FCSTD DOCUMENT  (FreeCAD 0.19R24276 (Git))
Label: base-20x20
License: All rights reserved
LicenseURL: http://en.wikipedia.org/wiki/All_rights_reserved
objects: Sketcher::SketchObject×1, PartDesign::Body×1
note: 2 computed .brp shape members not serialized (recipe doc carries the construction recipe); baked Part::Feature solids carry a one-line shape summary decoded from their .brp

FEATURE [Sketcher::SketchObject] Sketch  label="v2020"
  FullyConstrained = true
  MapMode = 5
  Support = -> [XY_Plane]
  sketch-geometry (45):
    g0: Circle CenterX=0 CenterY=0 CenterZ=0 NormalX=0 NormalY=0 NormalZ=1 AngleXU=0 Radius=2.5
    g1: LineSegment StartX=-3 StartY=4 StartZ=0 EndX=3 EndY=4 EndZ=0
    g2: LineSegment StartX=3 StartY=4 StartZ=0 EndX=5.1 EndY=6.1 EndZ=0
    g3: LineSegment StartX=5.1 StartY=6.1 StartZ=0 EndX=5.1 EndY=8.2 EndZ=0
    g4: LineSegment StartX=5.1 StartY=8.2 StartZ=0 EndX=3 EndY=8.2 EndZ=0
    g5: LineSegment StartX=3 StartY=8.2 StartZ=0 EndX=4.8 EndY=10 EndZ=0
    g6: LineSegment StartX=4.8 StartY=10 StartZ=0 EndX=10 EndY=10 EndZ=0
    g7: LineSegment StartX=10 StartY=10 StartZ=0 EndX=10 EndY=4.8 EndZ=0
    g8: LineSegment StartX=10 StartY=4.8 StartZ=0 EndX=8.2 EndY=3 EndZ=0
    g9: LineSegment StartX=8.2 StartY=3 StartZ=0 EndX=8.2 EndY=5.1 EndZ=0
    g10: LineSegment StartX=8.2 StartY=5.1 StartZ=0 EndX=6.1 EndY=5.1 EndZ=0
    g11: LineSegment StartX=6.1 StartY=5.1 StartZ=0 EndX=4 EndY=3 EndZ=0
    g12: LineSegment StartX=4 StartY=3 StartZ=0 EndX=4 EndY=-3 EndZ=0
    g13: LineSegment StartX=4 StartY=-3 StartZ=0 EndX=6.1 EndY=-5.1 EndZ=0
    g14: LineSegment StartX=6.1 StartY=-5.1 StartZ=0 EndX=8.2 EndY=-5.1 EndZ=0
    g15: LineSegment StartX=8.2 StartY=-5.1 StartZ=0 EndX=8.2 EndY=-3 EndZ=0
    g16: LineSegment StartX=8.2 StartY=-3 StartZ=0 EndX=10 EndY=-4.8 EndZ=0
    g17: LineSegment StartX=10 StartY=-4.8 StartZ=0 EndX=10 EndY=-10 EndZ=0
    g18: LineSegment StartX=10 StartY=-10 StartZ=0 EndX=4.8 EndY=-10 EndZ=0
    g19: LineSegment StartX=4.8 StartY=-10 StartZ=0 EndX=3 EndY=-8.2 EndZ=0
    g20: LineSegment StartX=3 StartY=-8.2 StartZ=0 EndX=5.1 EndY=-8.2 EndZ=0
    g21: LineSegment StartX=5.1 StartY=-8.2 StartZ=0 EndX=5.1 EndY=-6.1 EndZ=0
    g22: LineSegment StartX=5.1 StartY=-6.1 StartZ=0 EndX=3 EndY=-4 EndZ=0
    g23: LineSegment StartX=3 StartY=-4 StartZ=0 EndX=-3 EndY=-4 EndZ=0
    g24: LineSegment StartX=-3 StartY=-4 StartZ=0 EndX=-5.1 EndY=-6.1 EndZ=0
    g25: LineSegment StartX=-5.1 StartY=-6.1 StartZ=0 EndX=-5.1 EndY=-8.2 EndZ=0
    g26: LineSegment StartX=-5.1 StartY=-8.2 StartZ=0 EndX=-3 EndY=-8.2 EndZ=0
    g27: LineSegment StartX=-3 StartY=-8.2 StartZ=0 EndX=-4.8 EndY=-10 EndZ=0
    g28: LineSegment StartX=-4.8 StartY=-10 StartZ=0 EndX=-10 EndY=-10 EndZ=0
    g29: LineSegment StartX=-10 StartY=-10 StartZ=0 EndX=-10 EndY=-4.8 EndZ=0
    g30: LineSegment StartX=-10 StartY=-4.8 StartZ=0 EndX=-8.2 EndY=-3 EndZ=0
    g31: LineSegment StartX=-8.2 StartY=-3 StartZ=0 EndX=-8.2 EndY=-5.1 EndZ=0
    g32: LineSegment StartX=-8.2 StartY=-5.1 StartZ=0 EndX=-6.1 EndY=-5.1 EndZ=0
    g33: LineSegment StartX=-6.1 StartY=-5.1 StartZ=0 EndX=-4 EndY=-3 EndZ=0
    g34: LineSegment StartX=-4 StartY=-3 StartZ=0 EndX=-4 EndY=3 EndZ=0
    g35: LineSegment StartX=-4 StartY=3 StartZ=0 EndX=-6.1 EndY=5.1 EndZ=0
    g36: LineSegment StartX=-6.1 StartY=5.1 StartZ=0 EndX=-8.2 EndY=5.1 EndZ=0
    g37: LineSegment StartX=-8.2 StartY=5.1 StartZ=0 EndX=-8.2 EndY=3 EndZ=0
    g38: LineSegment StartX=-8.2 StartY=3 StartZ=0 EndX=-10 EndY=4.8 EndZ=0
    g39: LineSegment StartX=-10 StartY=4.8 StartZ=0 EndX=-10 EndY=10 EndZ=0
    g40: LineSegment StartX=-10 StartY=10 StartZ=0 EndX=-4.8 EndY=10 EndZ=0
    g41: LineSegment StartX=-4.8 StartY=10 StartZ=0 EndX=-3 EndY=8.2 EndZ=0
    g42: LineSegment StartX=-3 StartY=8.2 StartZ=0 EndX=-5.1 EndY=8.2 EndZ=0
    g43: LineSegment StartX=-5.1 StartY=8.2 StartZ=0 EndX=-5.1 EndY=6.1 EndZ=0
    g44: LineSegment StartX=-5.1 StartY=6.1 StartZ=0 EndX=-3 EndY=4 EndZ=0
  constraints (134):
    c: Coincident(g0,g-1)
    c: Diameter(g0) = 5
    c: Horizontal(g1)
    c: Coincident(g1,g2)
    c: Coincident(g2,g3)
    c: Vertical(g3)
    c: Coincident(g3,g4)
    c: Coincident(g4,g5)
    c: Coincident(g5,g6)
    c: Horizontal(g6)
    c: Coincident(g6,g7)
    c: Vertical(g7)
    c: Coincident(g7,g8)
    c: Coincident(g8,g9)
    c: Vertical(g9)
    c: Coincident(g9,g10)
    c: Horizontal(g10)
    c: Coincident(g10,g11)
    c: Coincident(g11,g12)
    c: Vertical(g12)
    c: Coincident(g12,g13)
    c: Coincident(g13,g14)
    c: Horizontal(g14)
    c: Coincident(g14,g15)
    c: Vertical(g15)
    c: Coincident(g15,g16)
    c: Coincident(g16,g17)
    c: Vertical(g17)
    c: Coincident(g17,g18)
    c: Horizontal(g18)
    c: Coincident(g18,g19)
    c: Coincident(g19,g20)
    c: Horizontal(g20)
    c: Coincident(g20,g21)
    c: Vertical(g21)
    c: Coincident(g21,g22)
    c: Coincident(g22,g23)
    c: Horizontal(g23)
    c: Coincident(g23,g24)
    c: Coincident(g24,g25)
    c: Vertical(g25)
    c: Coincident(g25,g26)
    c: Horizontal(g26)
    c: Coincident(g26,g27)
    c: Coincident(g27,g28)
    c: Horizontal(g28)
    c: Coincident(g28,g29)
    c: Vertical(g29)
    c: Coincident(g29,g30)
    c: Coincident(g30,g31)
    c: Vertical(g31)
    c: Coincident(g31,g32)
    c: Horizontal(g32)
    c: Coincident(g32,g33)
    c: Coincident(g33,g34)
    c: Vertical(g34)
    c: Coincident(g34,g35)
    c: Coincident(g35,g36)
    c: Horizontal(g36)
    c: Coincident(g36,g37)
    c: Vertical(g37)
    c: Coincident(g37,g38)
    c: Coincident(g38,g39)
    c: Vertical(g39)
    c: Coincident(g39,g40)
    c: Horizontal(g40)
    c: Coincident(g40,g41)
    c: Coincident(g41,g42)
    c: Horizontal(g42)
    c: Coincident(g42,g43)
    c: Coincident(g43,g44)
    c: Coincident(g44,g1)
    c: Equal(g44,g2)
    c: Equal(g11,g13)
    c: Equal(g22,g24)
    c: Equal(g33,g35)
    c: Equal(g44,g35)
    c: Equal(g24,g33)
    c: Equal(g22,g13)
    c: Parallel(g2,g11)
    c: Parallel(g13,g22)
    c: Parallel(g24,g33)
    c: Parallel(g35,g44)
    c: Angle(g24,g22) = 1.5708
    c: Angle(g2,g44) = 1.5708
    c: Angle(g35,g33) = 1.5708
    c: Equal(g34,g12)
    c: Equal(g1,g23)
    c: Equal(g12,g23)
    c: Equal(g10,g9)
    c: Equal(g3,g4)
    c: Horizontal(g4)
    c: Equal(g42,g43)
    c: Vertical(g43)
    c: Equal(g36,g37)
    c: Equal(g31,g32)
    c: Equal(g25,g26)
    c: Equal(g21,g20)
    c: Equal(g14,g15)
    c: Equal(g30,g38)
    c: Equal(g27,g19)
    c: Equal(g16,g8)
    c: Equal(g5,g41)
    c: Equal(g41,g38)
    c: Equal(g30,g27)
    c: Equal(g19,g16)
    c: Angle(g38,g30) = 1.5708
    c: Angle(g27,g19) = 1.5708
    c: Angle(g5,g41) = 1.5708
    c: Angle(g16,g8) = 1.5708
    c: Parallel(g30,g33)
    c: Parallel(g24,g27)
    c: Parallel(g13,g16)
    c: Equal(g21,g25)
    c: Equal(g32,g36)
    c: Equal(g10,g14)
    c: Equal(g3,g43)
    c: Equal(g40,g6)
    c: Equal(g39,g40)
    c: Equal(g6,g7)
    c: Equal(g17,g18)
    c: Equal(g29,g28)
    c: Equal(g29,g39)
    c: Equal(g17,g7)
    c: Parallel(g41,g38)
    c: DistanceX(g34,g11) = 8
    c: DistanceX(g39,g6) = 20
    c: DistanceY(g17,g6) = 20
    c: DistanceX(g38,g36) = 1.8
    c: Angle(g-1,g38) = 2.35619
    c: DistanceY(g29,g38) = 9.6
    c: DistanceY(g33,g34) = 6
    c: DistanceX(g34,g0) = 4
    c: DistanceY(g0,g1) = 4
FEATURE [PartDesign::Body] Body
  Group = -> [Sketch]
  Origin = -> Origin
